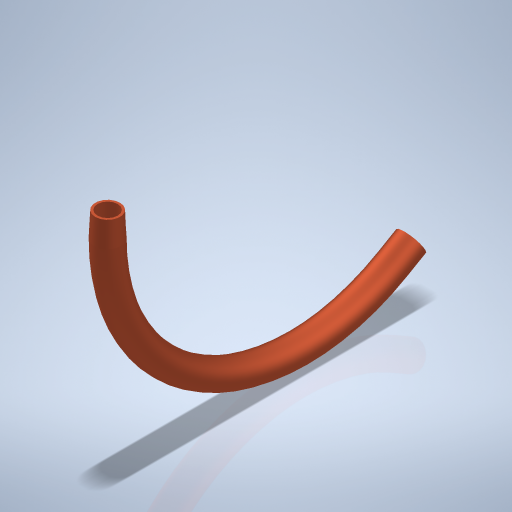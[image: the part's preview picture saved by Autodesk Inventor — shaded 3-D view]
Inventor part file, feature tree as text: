
AUTODESK INVENTOR PART (.ipt)
format: ipt  version: 2024 (Build 280153000, 153)  size: 307,200 bytes
history: native  units: mm
features: sketch x4, plane x2, loft x1, sweep x1, shell x1
ambient origin geometry x8: Origin, YZ Plane, XZ Plane, XY Plane, X Axis, Y Axis, Z Axis, Center Point
bodies: Body1 (feature_tree)
feature tree (9):
  sketch  "Skizze1"  dims[d0=5.5mm d3=5.5mm]
  sketch  "Skizze2"  dims[d4=42.3mm d5=4.7mm d10=-5.5mm]
  plane  "Arbeitsebene1"
  sketch  "Skizze3"  dims[d11=6.0mm]
  plane  "Arbeitsebene2"
  sketch  "Skizze4"  dims[d18=0.0mm d19=90.0deg d20=0.0mm d21=90.0deg d22=0.0mm d23=0.0mm d24=0.5mm d27=60.0deg]
  loft  "Erhebung2"
  sweep  "Sweeping3"
  shell  "Wandung2"  Thickness=-5.5mm
